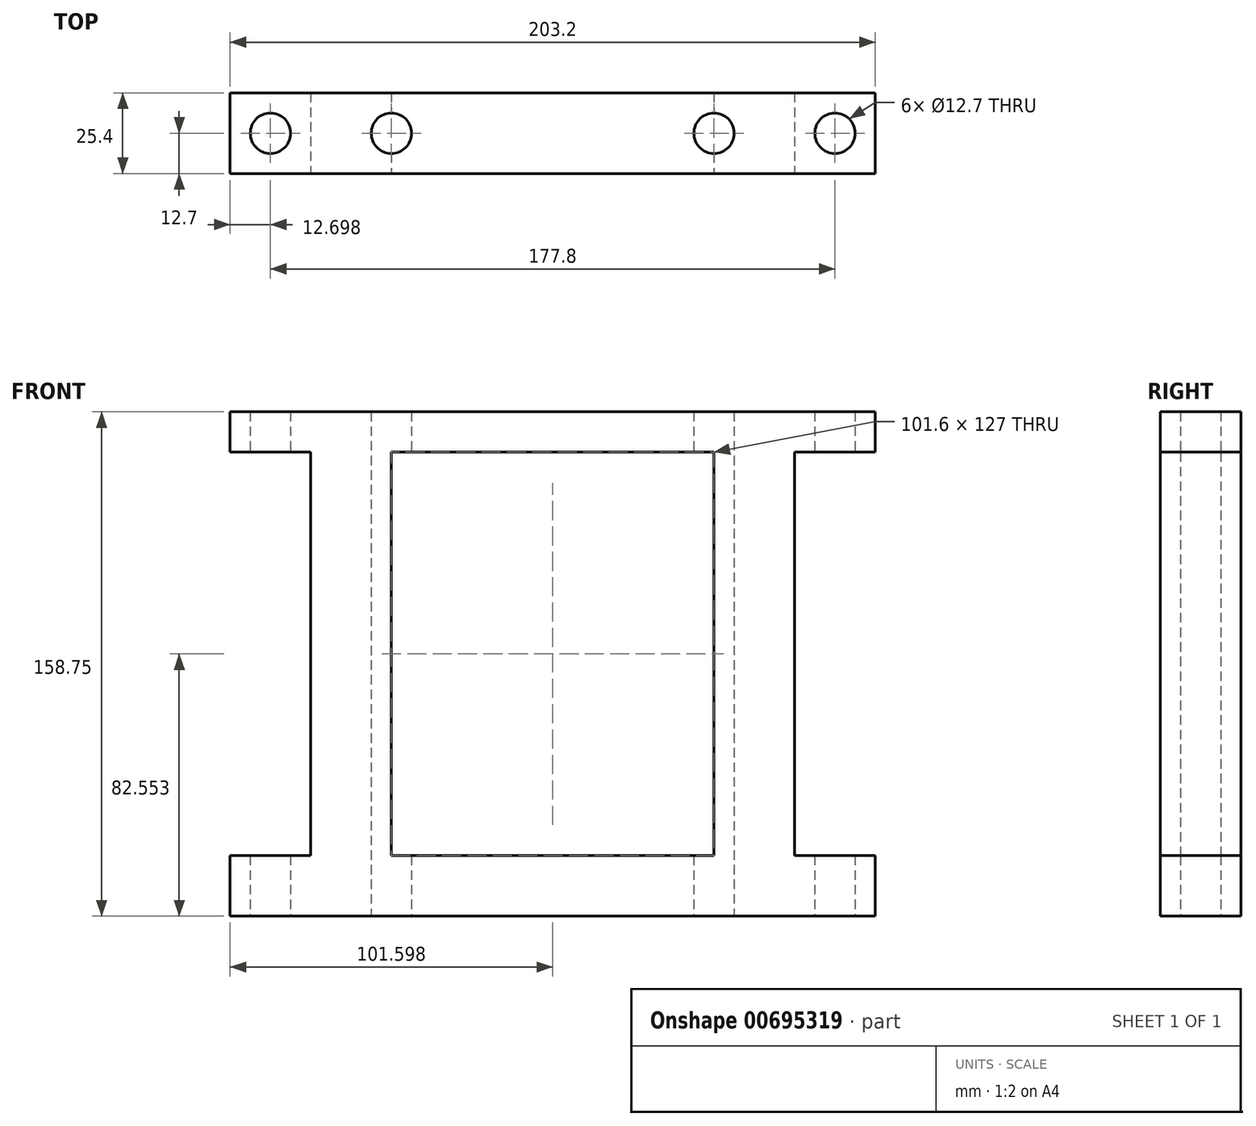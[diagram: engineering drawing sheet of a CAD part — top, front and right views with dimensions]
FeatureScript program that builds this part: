
annotation { "Feature Type Name" : "Feature", "Feature Type Description" : "" }
export const myFeature = defineFeature(function(context is Context, id is Id, definition is map)
    precondition{}
    {
        {
            var Q0;
            Q0=qCreatedBy(makeId("Front.planeOp"),FACE);
            var sketch = newSketch(context, id + "F0", { "sketchPlane" : qUnion([Q0])});
            skLineSegment(sketch, "E0.bottom", {"start": v(-94.94, 107.04) * mm, "end": v(108.26, 107.04) * mm});
            skLineSegment(sketch, "E0.top", {"start": v(-94.94, -51.7) * mm, "end": v(108.26, -51.7) * mm});
            skLineSegment(sketch, "E0.left", {"start": v(-94.94, 107.04) * mm, "end": v(-94.94, -51.7) * mm});
            skLineSegment(sketch, "E0.right", {"start": v(108.26, 107.04) * mm, "end": v(108.26, -51.7) * mm});
            skSolve(sketch);
        }
        {
            var Q0;
            Q0=makeQuery(id+"F0.imprint","IMPRINT",FACE,{"disambiguationData":[TD([[makeQuery(id+"F0.imprint","IMPRINT",EDGE,{"derivedFrom":sQuery(id+"F0.wireOp",EDGE,"E0.bottom")}),-1.0]])]});
            extrude(context, id + "F1", {"entities" : qUnion([Q0]), "depth" : 25.4 * mm, "offsetDistance" : 25.4 * mm});
        }
        {
            var Q0;
            Q0=makeQuery(id+"F1.opExtrude","CAP_FACE",FACE,{"disambiguationData":[OSD([sQuery(id+"F0.wireOp",EDGE,"E0.bottom"),sQuery(id+"F0.wireOp",EDGE,"E0.top"),sQuery(id+"F0.wireOp",EDGE,"E0.left"),sQuery(id+"F0.wireOp",EDGE,"E0.right")])],"isStart":false});
            var sketch = newSketch(context, id + "F2", { "sketchPlane" : qUnion([Q0])});
            skLineSegment(sketch, "E1.bottom", {"start": v(-94.94, 94.34) * mm, "end": v(-69.54, 94.34) * mm});
            skLineSegment(sketch, "E1.top", {"start": v(-94.94, -32.66) * mm, "end": v(-69.54, -32.66) * mm});
            skLineSegment(sketch, "E1.left", {"start": v(-94.94, 94.34) * mm, "end": v(-94.94, -32.66) * mm});
            skLineSegment(sketch, "E1.right", {"start": v(-69.54, 94.34) * mm, "end": v(-69.54, -32.66) * mm});
            skLineSegment(sketch, "E2.bottom", {"start": v(108.26, 94.34) * mm, "end": v(82.86, 94.34) * mm});
            skLineSegment(sketch, "E2.top", {"start": v(108.26, -32.66) * mm, "end": v(82.86, -32.66) * mm});
            skLineSegment(sketch, "E2.left", {"start": v(108.26, 94.34) * mm, "end": v(108.26, -32.66) * mm});
            skLineSegment(sketch, "E2.right", {"start": v(82.86, 94.34) * mm, "end": v(82.86, -32.66) * mm});
            skSolve(sketch);
        }
        {
            var Q0;
            Q0=makeQuery(id+"F2.imprint","IMPRINT",FACE,{"disambiguationData":[TD([[makeQuery(id+"F2.imprint","IMPRINT",EDGE,{"derivedFrom":sQuery(id+"F2.wireOp",EDGE,"E1.bottom")}),-1.0]])]});
            var Q1;
            Q1=makeQuery(id+"F2.imprint","IMPRINT",FACE,{"disambiguationData":[TD([[makeQuery(id+"F2.imprint","IMPRINT",EDGE,{"derivedFrom":sQuery(id+"F2.wireOp",EDGE,"E2.bottom")}),1.0]])]});
            extrude(context, id + "F3", {"entities" : qUnion([Q0, Q1]), "operationType" : NewBodyOperationType.REMOVE, "oppositeDirection" : true, "depth" : 25.4 * mm, "offsetDistance" : 25.4 * mm});
        }
        {
            var Q0;
            Q0=makeQuery(id+"F1.opExtrude","SWEPT_FACE",FACE,{"disambiguationData":[OSD([sQuery(id+"F0.wireOp",EDGE,"E0.top")])]});
            var sketch = newSketch(context, id + "F4", { "sketchPlane" : qUnion([Q0])});
            skCircle(sketch, "E3", {"center": v(-44.14, 12.7) * mm, "radius": 6.35 * mm});
            skPoint(sketch, "E3.centerSnap0", {"position": v(-94.94, 12.7) * mm});
            skCircle(sketch, "E4", {"center": v(57.46, 12.7) * mm, "radius": 6.35 * mm});
            skPoint(sketch, "E4.centerSnap0", {"position": v(108.26, 12.7) * mm});
            skSolve(sketch);
        }
        {
            var Q0;
            Q0=makeQuery(id+"F4.imprint","IMPRINT",FACE,{"disambiguationData":[TD([[makeQuery(id+"F4.imprint","IMPRINT",EDGE,{"derivedFrom":sQuery(id+"F4.wireOp",EDGE,"E3")}),1.0]])]});
            var Q1;
            Q1=makeQuery(id+"F4.imprint","IMPRINT",FACE,{"disambiguationData":[TD([[makeQuery(id+"F4.imprint","IMPRINT",EDGE,{"derivedFrom":sQuery(id+"F4.wireOp",EDGE,"E4")}),1.0]])]});
            extrude(context, id + "F5", {"entities" : qUnion([Q0, Q1]), "operationType" : NewBodyOperationType.REMOVE, "oppositeDirection" : true, "depth" : 177.8 * mm, "offsetDistance" : 25.4 * mm});
        }
        {
            var Q0;
            Q0=makeQuery(id+"F1.opExtrude","SWEPT_FACE",FACE,{"disambiguationData":[OSD([sQuery(id+"F0.wireOp",EDGE,"E0.top")])]});
            var sketch = newSketch(context, id + "F6", { "sketchPlane" : qUnion([Q0])});
            skCircle(sketch, "E5", {"center": v(-82.24, 12.7) * mm, "radius": 6.35 * mm});
            skPoint(sketch, "E5.centerSnap0", {"position": v(-94.94, 12.7) * mm});
            skCircle(sketch, "E6", {"center": v(95.56, 12.7) * mm, "radius": 6.35 * mm});
            skPoint(sketch, "E6.centerSnap0", {"position": v(108.26, 12.7) * mm});
            skSolve(sketch);
        }
        {
            var Q0;
            Q0=makeQuery(id+"F6.imprint","IMPRINT",FACE,{"disambiguationData":[TD([[makeQuery(id+"F6.imprint","IMPRINT",EDGE,{"derivedFrom":sQuery(id+"F6.wireOp",EDGE,"E5")}),1.0]])]});
            var Q1;
            Q1=makeQuery(id+"F6.imprint","IMPRINT",FACE,{"disambiguationData":[TD([[makeQuery(id+"F6.imprint","IMPRINT",EDGE,{"derivedFrom":sQuery(id+"F6.wireOp",EDGE,"E6")}),1.0]])]});
            extrude(context, id + "F7", {"entities" : qUnion([Q0, Q1]), "operationType" : NewBodyOperationType.REMOVE, "oppositeDirection" : true, "depth" : 177.8 * mm, "offsetDistance" : 25.4 * mm});
        }
        {
            var Q0;
            Q0=makeQuery(id+"F1.opExtrude","CAP_FACE",FACE,{"disambiguationData":[OSD([sQuery(id+"F0.wireOp",EDGE,"E0.bottom"),sQuery(id+"F0.wireOp",EDGE,"E0.top"),sQuery(id+"F0.wireOp",EDGE,"E0.left"),sQuery(id+"F0.wireOp",EDGE,"E0.right")])],"isStart":false});
            var sketch = newSketch(context, id + "F8", { "sketchPlane" : qUnion([Q0])});
            skLineSegment(sketch, "E7.bottom", {"start": v(-44.14, 94.34) * mm, "end": v(57.46, 94.34) * mm});
            skLineSegment(sketch, "E7.top", {"start": v(-44.14, -32.66) * mm, "end": v(57.46, -32.66) * mm});
            skLineSegment(sketch, "E7.left", {"start": v(-44.14, 94.34) * mm, "end": v(-44.14, -32.66) * mm});
            skLineSegment(sketch, "E7.right", {"start": v(57.46, 94.34) * mm, "end": v(57.46, -32.66) * mm});
            skSolve(sketch);
        }
        {
            var Q0;
            Q0=makeQuery(id+"F8.imprint","IMPRINT",FACE,{"disambiguationData":[TD([[makeQuery(id+"F8.imprint","IMPRINT",EDGE,{"derivedFrom":sQuery(id+"F8.wireOp",EDGE,"E7.bottom")}),-1.0]])]});
            extrude(context, id + "F9", {"entities" : qUnion([Q0]), "operationType" : NewBodyOperationType.REMOVE, "oppositeDirection" : true, "depth" : 25.4 * mm, "offsetDistance" : 25.4 * mm});
        }
    });
